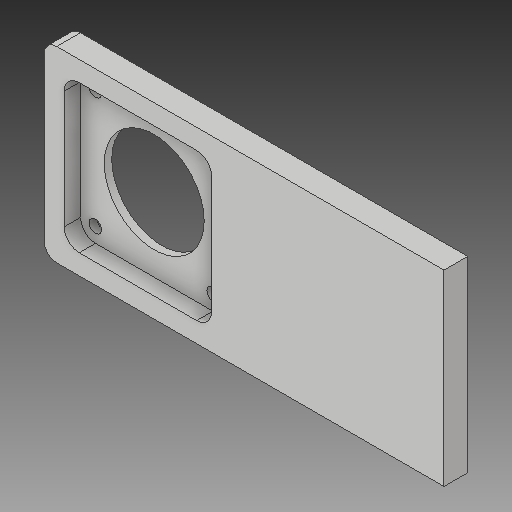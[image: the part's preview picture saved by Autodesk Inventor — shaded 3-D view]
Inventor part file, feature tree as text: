
AUTODESK INVENTOR PART (.ipt)
format: ipt  version: 2018 (Build 220112000, 112)  size: 129,536 bytes
history: native  units: mm
features: other x4, sketch x3
ambient origin geometry x8: Origin, YZ Plane, XZ Plane, XY Plane, X Axis, Y Axis, Z Axis, Center Point
bodies: Body1 (feature_tree)
feature tree (7):
  other  "SUPORTE_MOTOR_EIXO_Y_1.ipt"
  other  "Sólido1::SUPORTE_MOTOR_EIXO_Y_1.ipt"
  other  "OperaçãoIdentificador1"
  sketch  "Esboço1"  dims[d0=10.0mm]
  sketch  "Esboço9"
  sketch  "Esboço10"
  other  "Sólido1"
